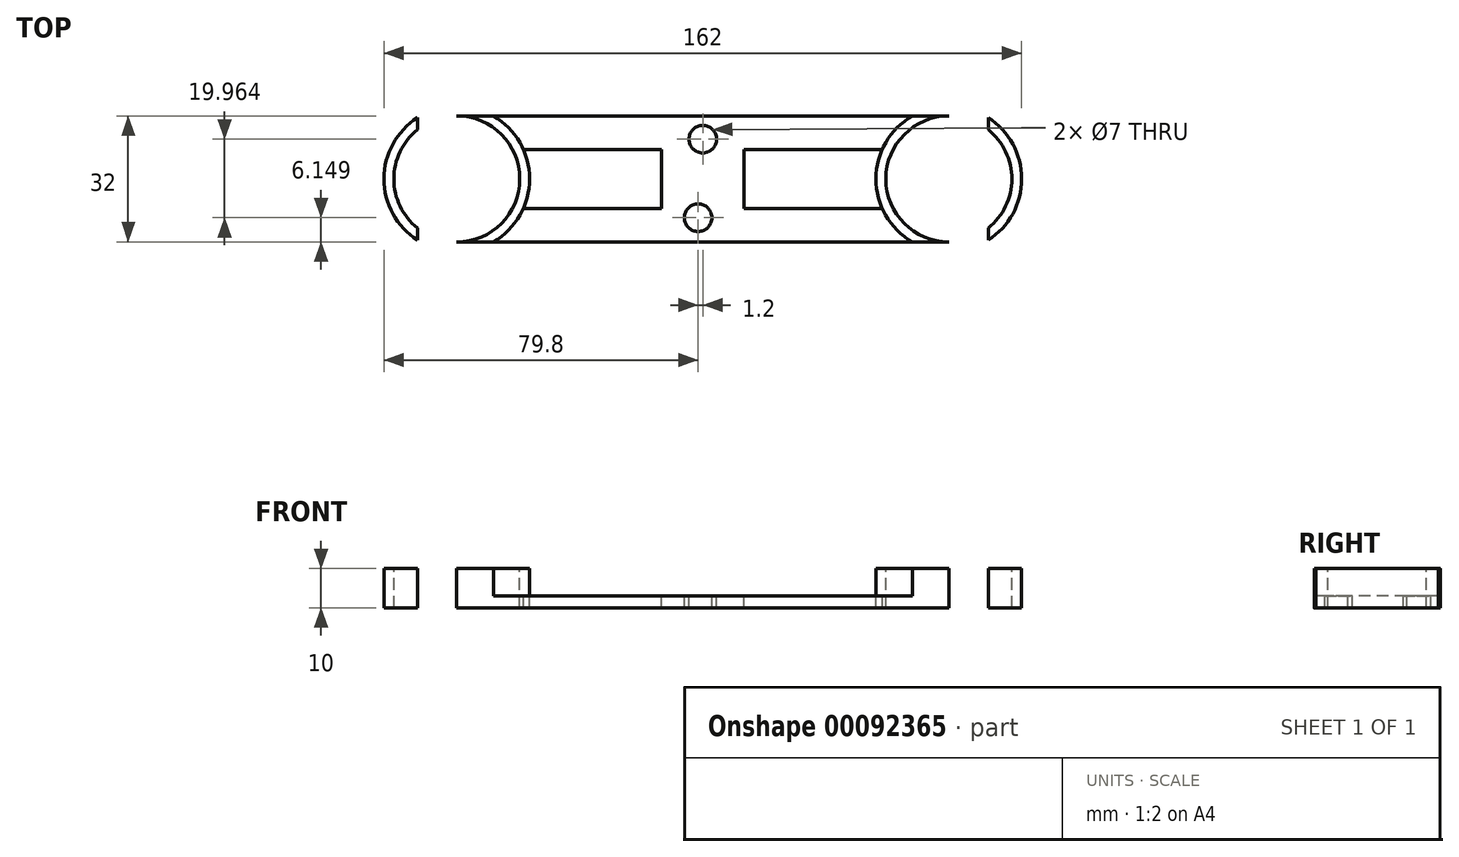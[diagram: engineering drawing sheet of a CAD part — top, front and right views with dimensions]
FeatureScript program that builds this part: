
annotation { "Feature Type Name" : "Feature", "Feature Type Description" : "" }
export const myFeature = defineFeature(function(context is Context, id is Id, definition is map)
    precondition{}
    {
        {
            var Q0;
            Q0=qCreatedBy(makeId("Top.planeOp"),FACE);
            var sketch = newSketch(context, id + "F0", { "sketchPlane" : qUnion([Q0])});
            skLineSegment(sketch, "E0.bottom", {"start": v(-62.5, 7.5) * mm, "end": v(62.5, 7.5) * mm});
            skLineSegment(sketch, "E0.top", {"start": v(-62.5, -7.5) * mm, "end": v(62.5, -7.5) * mm});
            skLineSegment(sketch, "E0.left", {"start": v(-62.5, 7.5) * mm, "end": v(-62.5, -7.5) * mm});
            skLineSegment(sketch, "E0.right", {"start": v(62.5, 7.5) * mm, "end": v(62.5, -7.5) * mm});
            skLineSegment(sketch, "E1", {"start": v(0, 7.5) * mm, "end": v(0, -7.5) * mm, "construction": true});
            skLineSegment(sketch, "E2", {"start": v(62.5, 0) * mm, "end": v(0, 0) * mm, "construction": true});
            skLineSegment(sketch, "E3", {"start": v(0, 0) * mm, "end": v(-62.5, 0) * mm, "construction": true});
            skLineSegment(sketch, "E4.bottom", {"start": v(-46.5, 7.5) * mm, "end": v(46.5, 7.5) * mm, "construction": true});
            skLineSegment(sketch, "E4.top", {"start": v(-46.5, -7.5) * mm, "end": v(46.5, -7.5) * mm, "construction": true});
            skLineSegment(sketch, "E4.left", {"start": v(-46.5, 7.5) * mm, "end": v(-46.5, -7.5) * mm, "construction": true});
            skLineSegment(sketch, "E4.right", {"start": v(46.5, 7.5) * mm, "end": v(46.5, -7.5) * mm, "construction": true});
            skLineSegment(sketch, "E5", {"start": v(-46.5, 18.61) * mm, "end": v(-62.5, 18.61) * mm, "construction": true});
            skLineSegment(sketch, "E6", {"start": v(46.5, 10.29) * mm, "end": v(62.5, 10.29) * mm, "construction": true});
            skCircle(sketch, "E7", {"center": v(62.5, 0) * mm, "radius": 16 * mm});
            skCircle(sketch, "E8", {"center": v(-62.5, 0) * mm, "radius": 16 * mm});
            skCircle(sketch, "E9", {"center": v(-62.5, 0) * mm, "radius": 18.5 * mm});
            skCircle(sketch, "E10", {"center": v(62.5, 0) * mm, "radius": 18.5 * mm});
            skLineSegment(sketch, "E11", {"start": v(-72.5, 15.56) * mm, "end": v(-72.5, -15.56) * mm});
            skLineSegment(sketch, "E12", {"start": v(-62.5, 0) * mm, "end": v(-72.5, 0) * mm, "construction": true});
            skLineSegment(sketch, "E13", {"start": v(72.5, 15.56) * mm, "end": v(72.5, -15.56) * mm});
            skLineSegment(sketch, "E14", {"start": v(62.5, 0) * mm, "end": v(72.5, 0) * mm, "construction": true});
            skLineSegment(sketch, "E15.top", {"start": v(-62.5, 16) * mm, "end": v(62.5, 16) * mm});
            skLineSegment(sketch, "E15.left", {"start": v(-62.5, 7.5) * mm, "end": v(-62.5, 16) * mm});
            skLineSegment(sketch, "E15.right", {"start": v(62.5, 7.5) * mm, "end": v(62.5, 16) * mm});
            skLineSegment(sketch, "E16.bottom", {"start": v(62.5, -7.5) * mm, "end": v(-62.5, -7.5) * mm});
            skLineSegment(sketch, "E16.top", {"start": v(62.5, -16) * mm, "end": v(-62.5, -16) * mm});
            skLineSegment(sketch, "E16.left", {"start": v(62.5, -7.5) * mm, "end": v(62.5, -16) * mm});
            skLineSegment(sketch, "E16.right", {"start": v(-62.5, -7.5) * mm, "end": v(-62.5, -16) * mm});
            skLineSegment(sketch, "E17", {"start": v(-10.45, 7.5) * mm, "end": v(-10.45, -7.5) * mm});
            skLineSegment(sketch, "E18", {"start": v(10.45, 7.5) * mm, "end": v(10.45, -7.5) * mm});
            skLineSegment(sketch, "E19", {"start": v(-10.45, 3.44) * mm, "end": v(0, 3.44) * mm, "construction": true});
            skLineSegment(sketch, "E20", {"start": v(0, 3.44) * mm, "end": v(10.45, 3.44) * mm, "construction": true});
            skSolve(sketch);
        }
        {
            var Q0;
            {var subQ3=sQuery(id+"F0.wireOp",EDGE,"E11");var subQ5=sQuery(id+"F0.wireOp",EDGE,"E9");var subQ6=makeQuery(id+"F0.imprint","INTERSECT",VERTEX,{"disambiguationData":[OD(0.0)],"derivedFrom":[subQ5,subQ3]});Q0=makeQuery(id+"F0.imprint","IMPRINT",FACE,{"disambiguationData":[TD([[makeQuery(id+"F0.imprint","IMPRINT",EDGE,{"disambiguationData":[TD([[subQ6,1.0]])],"derivedFrom":subQ5}),1.0]])]});}
            var Q1;
            {var subQ3=sQuery(id+"F0.wireOp",EDGE,"E11");var subQ5=sQuery(id+"F0.wireOp",EDGE,"E9");var subQ6=makeQuery(id+"F0.imprint","INTERSECT",VERTEX,{"disambiguationData":[OD(1.0)],"derivedFrom":[subQ5,subQ3]});Q1=makeQuery(id+"F0.imprint","IMPRINT",FACE,{"disambiguationData":[TD([[makeQuery(id+"F0.imprint","IMPRINT",EDGE,{"disambiguationData":[TD([[subQ6,-1.0]])],"derivedFrom":subQ5}),1.0]])]});}
            var Q2;
            {var subQ0=sQuery(id+"F0.wireOp",EDGE,"E15.top");var subQ5=sQuery(id+"F0.wireOp",EDGE,"E9");var subQ6=makeQuery(id+"F0.imprint","INTERSECT",VERTEX,{"derivedFrom":[subQ5,subQ0]});Q2=makeQuery(id+"F0.imprint","IMPRINT",FACE,{"disambiguationData":[TD([[makeQuery(id+"F0.imprint","IMPRINT",EDGE,{"disambiguationData":[TD([[subQ6,1.0]])],"derivedFrom":subQ5}),1.0]])]});}
            var Q3;
            {var subQ0=sQuery(id+"F0.wireOp",EDGE,"E16.top");var subQ5=sQuery(id+"F0.wireOp",EDGE,"E9");var subQ7=makeQuery(id+"F0.imprint","INTERSECT",VERTEX,{"derivedFrom":[subQ5,subQ0]});Q3=makeQuery(id+"F0.imprint","IMPRINT",FACE,{"disambiguationData":[TD([[makeQuery(id+"F0.imprint","IMPRINT",EDGE,{"disambiguationData":[TD([[subQ7,-1.0]])],"derivedFrom":subQ5}),1.0]])]});}
            var Q4;
            {var subQ0=sQuery(id+"F0.wireOp",EDGE,"E0.bottom");var subQ1=sQuery(id+"F0.wireOp",EDGE,"E8");var subQ2=makeQuery(id+"F0.imprint","INTERSECT",VERTEX,{"derivedFrom":[subQ1,subQ0]});Q4=makeQuery(id+"F0.imprint","IMPRINT",FACE,{"disambiguationData":[TD([[makeQuery(id+"F0.imprint","IMPRINT",EDGE,{"disambiguationData":[TD([[subQ2,1.0]])],"derivedFrom":subQ1}),-1.0]])]});}
            var Q5;
            {var subQ3=sQuery(id+"F0.wireOp",EDGE,"E11");var subQ5=sQuery(id+"F0.wireOp",EDGE,"E9");var subQ6=makeQuery(id+"F0.imprint","INTERSECT",VERTEX,{"disambiguationData":[OD(1.0)],"derivedFrom":[subQ5,subQ3]});Q5=makeQuery(id+"F0.imprint","IMPRINT",FACE,{"disambiguationData":[TD([[makeQuery(id+"F0.imprint","IMPRINT",EDGE,{"disambiguationData":[TD([[subQ6,-1.0]])],"derivedFrom":subQ5}),1.0]])]});}
            var Q6;
            {var subQ3=sQuery(id+"F0.wireOp",EDGE,"E11");var subQ5=sQuery(id+"F0.wireOp",EDGE,"E9");var subQ6=makeQuery(id+"F0.imprint","INTERSECT",VERTEX,{"disambiguationData":[OD(0.0)],"derivedFrom":[subQ5,subQ3]});Q6=makeQuery(id+"F0.imprint","IMPRINT",FACE,{"disambiguationData":[TD([[makeQuery(id+"F0.imprint","IMPRINT",EDGE,{"disambiguationData":[TD([[subQ6,1.0]])],"derivedFrom":subQ5}),1.0]])]});}
            var Q7;
            {var subQ3=sQuery(id+"F0.wireOp",EDGE,"E13");var subQ5=sQuery(id+"F0.wireOp",EDGE,"E10");var subQ7=makeQuery(id+"F0.imprint","INTERSECT",VERTEX,{"disambiguationData":[OD(0.0)],"derivedFrom":[subQ5,subQ3]});Q7=makeQuery(id+"F0.imprint","IMPRINT",FACE,{"disambiguationData":[TD([[makeQuery(id+"F0.imprint","IMPRINT",EDGE,{"disambiguationData":[TD([[subQ7,-1.0]])],"derivedFrom":subQ5}),1.0]])]});}
            var Q8;
            {var subQ3=sQuery(id+"F0.wireOp",EDGE,"E13");var subQ5=sQuery(id+"F0.wireOp",EDGE,"E10");var subQ7=makeQuery(id+"F0.imprint","INTERSECT",VERTEX,{"disambiguationData":[OD(0.0)],"derivedFrom":[subQ5,subQ3]});Q8=makeQuery(id+"F0.imprint","IMPRINT",FACE,{"disambiguationData":[TD([[makeQuery(id+"F0.imprint","IMPRINT",EDGE,{"disambiguationData":[TD([[subQ7,-1.0]])],"derivedFrom":subQ5}),1.0]])]});}
            var Q9;
            {var subQ3=sQuery(id+"F0.wireOp",EDGE,"E13");var subQ5=sQuery(id+"F0.wireOp",EDGE,"E10");var subQ6=makeQuery(id+"F0.imprint","INTERSECT",VERTEX,{"disambiguationData":[OD(1.0)],"derivedFrom":[subQ5,subQ3]});Q9=makeQuery(id+"F0.imprint","IMPRINT",FACE,{"disambiguationData":[TD([[makeQuery(id+"F0.imprint","IMPRINT",EDGE,{"disambiguationData":[TD([[subQ6,1.0]])],"derivedFrom":subQ5}),1.0]])]});}
            var Q10;
            {var subQ0=sQuery(id+"F0.wireOp",EDGE,"E15.top");var subQ5=sQuery(id+"F0.wireOp",EDGE,"E10");var subQ6=makeQuery(id+"F0.imprint","INTERSECT",VERTEX,{"derivedFrom":[subQ5,subQ0]});Q10=makeQuery(id+"F0.imprint","IMPRINT",FACE,{"disambiguationData":[TD([[makeQuery(id+"F0.imprint","IMPRINT",EDGE,{"disambiguationData":[TD([[subQ6,-1.0]])],"derivedFrom":subQ5}),1.0]])]});}
            var Q11;
            {var subQ0=sQuery(id+"F0.wireOp",EDGE,"E0.bottom");var subQ1=sQuery(id+"F0.wireOp",EDGE,"E7");var subQ2=makeQuery(id+"F0.imprint","INTERSECT",VERTEX,{"derivedFrom":[subQ1,subQ0]});Q11=makeQuery(id+"F0.imprint","IMPRINT",FACE,{"disambiguationData":[TD([[makeQuery(id+"F0.imprint","IMPRINT",EDGE,{"disambiguationData":[TD([[subQ2,-1.0]])],"derivedFrom":subQ1}),-1.0]])]});}
            var Q12;
            {var subQ0=sQuery(id+"F0.wireOp",EDGE,"E16.top");var subQ5=sQuery(id+"F0.wireOp",EDGE,"E10");var subQ6=makeQuery(id+"F0.imprint","INTERSECT",VERTEX,{"derivedFrom":[subQ5,subQ0]});Q12=makeQuery(id+"F0.imprint","IMPRINT",FACE,{"disambiguationData":[TD([[makeQuery(id+"F0.imprint","IMPRINT",EDGE,{"disambiguationData":[TD([[subQ6,1.0]])],"derivedFrom":subQ5}),1.0]])]});}
            var Q13;
            {var subQ3=sQuery(id+"F0.wireOp",EDGE,"E13");var subQ5=sQuery(id+"F0.wireOp",EDGE,"E10");var subQ6=makeQuery(id+"F0.imprint","INTERSECT",VERTEX,{"disambiguationData":[OD(1.0)],"derivedFrom":[subQ5,subQ3]});Q13=makeQuery(id+"F0.imprint","IMPRINT",FACE,{"disambiguationData":[TD([[makeQuery(id+"F0.imprint","IMPRINT",EDGE,{"disambiguationData":[TD([[subQ6,1.0]])],"derivedFrom":subQ5}),1.0]])]});}
            var Q14;
            {var subQ0=sQuery(id+"F0.wireOp",EDGE,"E16.top");var subQ1=sQuery(id+"F0.wireOp",EDGE,"E9");var subQ2=makeQuery(id+"F0.imprint","INTERSECT",VERTEX,{"derivedFrom":[subQ1,subQ0]});Q14=makeQuery(id+"F0.imprint","IMPRINT",FACE,{"disambiguationData":[TD([[makeQuery(id+"F0.imprint","IMPRINT",EDGE,{"disambiguationData":[TD([[subQ2,-1.0]])],"derivedFrom":subQ1}),-1.0]])]});}
            var Q15;
            {var subQ0=sQuery(id+"F0.wireOp",EDGE,"E15.top");var subQ1=sQuery(id+"F0.wireOp",EDGE,"E9");var subQ2=makeQuery(id+"F0.imprint","INTERSECT",VERTEX,{"derivedFrom":[subQ1,subQ0]});Q15=makeQuery(id+"F0.imprint","IMPRINT",FACE,{"disambiguationData":[TD([[makeQuery(id+"F0.imprint","IMPRINT",EDGE,{"disambiguationData":[TD([[subQ2,1.0]])],"derivedFrom":subQ1}),-1.0]])]});}
            var Q16;
            {var subQ0=sQuery(id+"F0.wireOp",EDGE,"E17");Q16=makeQuery(id+"F0.imprint","IMPRINT",FACE,{"disambiguationData":[TD([[makeQuery(id+"F0.imprint","IMPRINT",EDGE,{"derivedFrom":subQ0}),1.0]])]});}
            extrude(context, id + "F1", {"entities" : qUnion([Q0, Q1, Q2, Q3, Q4, Q5, Q6, Q7, Q8, Q9, Q10, Q11, Q12, Q13, Q14, Q15, Q16]), "oppositeDirection" : true, "depth" : 5 * mm});
        }
        {
            var Q0;
            {var subQ3=sQuery(id+"F0.wireOp",EDGE,"E11");var subQ5=sQuery(id+"F0.wireOp",EDGE,"E9");var subQ6=makeQuery(id+"F0.imprint","INTERSECT",VERTEX,{"disambiguationData":[OD(0.0)],"derivedFrom":[subQ5,subQ3]});Q0=makeQuery(id+"F0.imprint","IMPRINT",FACE,{"disambiguationData":[TD([[makeQuery(id+"F0.imprint","IMPRINT",EDGE,{"disambiguationData":[TD([[subQ6,1.0]])],"derivedFrom":subQ5}),1.0]])]});}
            var Q1;
            {var subQ3=sQuery(id+"F0.wireOp",EDGE,"E11");var subQ5=sQuery(id+"F0.wireOp",EDGE,"E9");var subQ6=makeQuery(id+"F0.imprint","INTERSECT",VERTEX,{"disambiguationData":[OD(1.0)],"derivedFrom":[subQ5,subQ3]});Q1=makeQuery(id+"F0.imprint","IMPRINT",FACE,{"disambiguationData":[TD([[makeQuery(id+"F0.imprint","IMPRINT",EDGE,{"disambiguationData":[TD([[subQ6,-1.0]])],"derivedFrom":subQ5}),1.0]])]});}
            var Q2;
            {var subQ0=sQuery(id+"F0.wireOp",EDGE,"E15.top");var subQ5=sQuery(id+"F0.wireOp",EDGE,"E9");var subQ6=makeQuery(id+"F0.imprint","INTERSECT",VERTEX,{"derivedFrom":[subQ5,subQ0]});Q2=makeQuery(id+"F0.imprint","IMPRINT",FACE,{"disambiguationData":[TD([[makeQuery(id+"F0.imprint","IMPRINT",EDGE,{"disambiguationData":[TD([[subQ6,1.0]])],"derivedFrom":subQ5}),1.0]])]});}
            var Q3;
            {var subQ0=sQuery(id+"F0.wireOp",EDGE,"E16.top");var subQ5=sQuery(id+"F0.wireOp",EDGE,"E9");var subQ7=makeQuery(id+"F0.imprint","INTERSECT",VERTEX,{"derivedFrom":[subQ5,subQ0]});Q3=makeQuery(id+"F0.imprint","IMPRINT",FACE,{"disambiguationData":[TD([[makeQuery(id+"F0.imprint","IMPRINT",EDGE,{"disambiguationData":[TD([[subQ7,-1.0]])],"derivedFrom":subQ5}),1.0]])]});}
            var Q4;
            {var subQ0=sQuery(id+"F0.wireOp",EDGE,"E0.bottom");var subQ1=sQuery(id+"F0.wireOp",EDGE,"E8");var subQ2=makeQuery(id+"F0.imprint","INTERSECT",VERTEX,{"derivedFrom":[subQ1,subQ0]});Q4=makeQuery(id+"F0.imprint","IMPRINT",FACE,{"disambiguationData":[TD([[makeQuery(id+"F0.imprint","IMPRINT",EDGE,{"disambiguationData":[TD([[subQ2,1.0]])],"derivedFrom":subQ1}),-1.0]])]});}
            var Q5;
            {var subQ3=sQuery(id+"F0.wireOp",EDGE,"E11");var subQ5=sQuery(id+"F0.wireOp",EDGE,"E9");var subQ6=makeQuery(id+"F0.imprint","INTERSECT",VERTEX,{"disambiguationData":[OD(0.0)],"derivedFrom":[subQ5,subQ3]});Q5=makeQuery(id+"F0.imprint","IMPRINT",FACE,{"disambiguationData":[TD([[makeQuery(id+"F0.imprint","IMPRINT",EDGE,{"disambiguationData":[TD([[subQ6,1.0]])],"derivedFrom":subQ5}),1.0]])]});}
            var Q6;
            {var subQ3=sQuery(id+"F0.wireOp",EDGE,"E11");var subQ5=sQuery(id+"F0.wireOp",EDGE,"E9");var subQ6=makeQuery(id+"F0.imprint","INTERSECT",VERTEX,{"disambiguationData":[OD(1.0)],"derivedFrom":[subQ5,subQ3]});Q6=makeQuery(id+"F0.imprint","IMPRINT",FACE,{"disambiguationData":[TD([[makeQuery(id+"F0.imprint","IMPRINT",EDGE,{"disambiguationData":[TD([[subQ6,-1.0]])],"derivedFrom":subQ5}),1.0]])]});}
            var Q7;
            {var subQ3=sQuery(id+"F0.wireOp",EDGE,"E13");var subQ5=sQuery(id+"F0.wireOp",EDGE,"E10");var subQ6=makeQuery(id+"F0.imprint","INTERSECT",VERTEX,{"disambiguationData":[OD(1.0)],"derivedFrom":[subQ5,subQ3]});Q7=makeQuery(id+"F0.imprint","IMPRINT",FACE,{"disambiguationData":[TD([[makeQuery(id+"F0.imprint","IMPRINT",EDGE,{"disambiguationData":[TD([[subQ6,1.0]])],"derivedFrom":subQ5}),1.0]])]});}
            var Q8;
            {var subQ3=sQuery(id+"F0.wireOp",EDGE,"E13");var subQ5=sQuery(id+"F0.wireOp",EDGE,"E10");var subQ7=makeQuery(id+"F0.imprint","INTERSECT",VERTEX,{"disambiguationData":[OD(0.0)],"derivedFrom":[subQ5,subQ3]});Q8=makeQuery(id+"F0.imprint","IMPRINT",FACE,{"disambiguationData":[TD([[makeQuery(id+"F0.imprint","IMPRINT",EDGE,{"disambiguationData":[TD([[subQ7,-1.0]])],"derivedFrom":subQ5}),1.0]])]});}
            var Q9;
            {var subQ3=sQuery(id+"F0.wireOp",EDGE,"E13");var subQ5=sQuery(id+"F0.wireOp",EDGE,"E10");var subQ6=makeQuery(id+"F0.imprint","INTERSECT",VERTEX,{"disambiguationData":[OD(1.0)],"derivedFrom":[subQ5,subQ3]});Q9=makeQuery(id+"F0.imprint","IMPRINT",FACE,{"disambiguationData":[TD([[makeQuery(id+"F0.imprint","IMPRINT",EDGE,{"disambiguationData":[TD([[subQ6,1.0]])],"derivedFrom":subQ5}),1.0]])]});}
            var Q10;
            {var subQ0=sQuery(id+"F0.wireOp",EDGE,"E15.top");var subQ5=sQuery(id+"F0.wireOp",EDGE,"E10");var subQ6=makeQuery(id+"F0.imprint","INTERSECT",VERTEX,{"derivedFrom":[subQ5,subQ0]});Q10=makeQuery(id+"F0.imprint","IMPRINT",FACE,{"disambiguationData":[TD([[makeQuery(id+"F0.imprint","IMPRINT",EDGE,{"disambiguationData":[TD([[subQ6,-1.0]])],"derivedFrom":subQ5}),1.0]])]});}
            var Q11;
            {var subQ0=sQuery(id+"F0.wireOp",EDGE,"E0.bottom");var subQ1=sQuery(id+"F0.wireOp",EDGE,"E7");var subQ2=makeQuery(id+"F0.imprint","INTERSECT",VERTEX,{"derivedFrom":[subQ1,subQ0]});Q11=makeQuery(id+"F0.imprint","IMPRINT",FACE,{"disambiguationData":[TD([[makeQuery(id+"F0.imprint","IMPRINT",EDGE,{"disambiguationData":[TD([[subQ2,-1.0]])],"derivedFrom":subQ1}),-1.0]])]});}
            var Q12;
            {var subQ0=sQuery(id+"F0.wireOp",EDGE,"E16.top");var subQ5=sQuery(id+"F0.wireOp",EDGE,"E10");var subQ6=makeQuery(id+"F0.imprint","INTERSECT",VERTEX,{"derivedFrom":[subQ5,subQ0]});Q12=makeQuery(id+"F0.imprint","IMPRINT",FACE,{"disambiguationData":[TD([[makeQuery(id+"F0.imprint","IMPRINT",EDGE,{"disambiguationData":[TD([[subQ6,1.0]])],"derivedFrom":subQ5}),1.0]])]});}
            var Q13;
            {var subQ3=sQuery(id+"F0.wireOp",EDGE,"E13");var subQ5=sQuery(id+"F0.wireOp",EDGE,"E10");var subQ7=makeQuery(id+"F0.imprint","INTERSECT",VERTEX,{"disambiguationData":[OD(0.0)],"derivedFrom":[subQ5,subQ3]});Q13=makeQuery(id+"F0.imprint","IMPRINT",FACE,{"disambiguationData":[TD([[makeQuery(id+"F0.imprint","IMPRINT",EDGE,{"disambiguationData":[TD([[subQ7,-1.0]])],"derivedFrom":subQ5}),1.0]])]});}
            extrude(context, id + "F2", {"entities" : qUnion([Q0, Q1, Q2, Q3, Q4, Q5, Q6, Q7, Q8, Q9, Q10, Q11, Q12, Q13]), "operationType" : NewBodyOperationType.ADD, "depth" : 5 * mm});
        }
        {
            var Q0;
            Q0=makeQuery(id+"F1.opExtrude","CAP_FACE",FACE,{"disambiguationData":[OSD([sQuery(id+"F0.wireOp",EDGE,"E7"),sQuery(id+"F0.wireOp",EDGE,"E8"),sQuery(id+"F0.wireOp",EDGE,"E9"),sQuery(id+"F0.wireOp",EDGE,"E10"),sQuery(id+"F0.wireOp",EDGE,"E11"),sQuery(id+"F0.wireOp",EDGE,"E13"),sQuery(id+"F0.wireOp",EDGE,"E0.bottom"),sQuery(id+"F0.wireOp",EDGE,"E15.top"),sQuery(id+"F0.wireOp",EDGE,"E16.bottom"),sQuery(id+"F0.wireOp",EDGE,"E16.top"),sQuery(id+"F0.wireOp",EDGE,"E17"),sQuery(id+"F0.wireOp",EDGE,"E18")])],"isStart":true});
            var sketch = newSketch(context, id + "F3", { "sketchPlane" : qUnion([Q0])});
            skCircle(sketch, "E21", {"center": v(0, 10.11) * mm, "radius": 3.5 * mm});
            skCircle(sketch, "E22", {"center": v(-1.2, -9.85) * mm, "radius": 3.5 * mm});
            skLineSegment(sketch, "E23", {"start": v(0, 10.11) * mm, "end": v(-1.2, -9.85) * mm, "construction": true});
            skSolve(sketch);
        }
        {
            var Q0;
            Q0=makeQuery(id+"F3.imprint","IMPRINT",FACE,{"disambiguationData":[TD([[makeQuery(id+"F3.imprint","IMPRINT",EDGE,{"derivedFrom":sQuery(id+"F3.wireOp",EDGE,"E21")}),-1.0]])]});
            var Q1;
            Q1=makeQuery(id+"F3.imprint","IMPRINT",FACE,{"disambiguationData":[TD([[makeQuery(id+"F3.imprint","IMPRINT",EDGE,{"derivedFrom":sQuery(id+"F3.wireOp",EDGE,"E22")}),-1.0]])]});
            extrude(context, id + "F4", {"entities" : qUnion([Q0, Q1]), "operationType" : NewBodyOperationType.REMOVE, "oppositeDirection" : true, "depth" : 2 * mm});
        }
        {
            var Q0;
            Q0=makeQuery(id+"F4.boolean.opBoolean","SPLIT",FACE,{"disambiguationData":[TD([makeQuery(id+"F4.opExtrude","SWEPT_FACE",FACE,{"disambiguationData":[OSD([sQuery(id+"F3.wireOp",EDGE,"E21")])]})])],"derivedFrom":makeQuery(id+"F1.opExtrude","CAP_FACE",FACE,{"disambiguationData":[OSD([sQuery(id+"F0.wireOp",EDGE,"E7"),sQuery(id+"F0.wireOp",EDGE,"E8"),sQuery(id+"F0.wireOp",EDGE,"E9"),sQuery(id+"F0.wireOp",EDGE,"E10"),sQuery(id+"F0.wireOp",EDGE,"E11"),sQuery(id+"F0.wireOp",EDGE,"E13"),sQuery(id+"F0.wireOp",EDGE,"E0.bottom"),sQuery(id+"F0.wireOp",EDGE,"E15.top"),sQuery(id+"F0.wireOp",EDGE,"E16.bottom"),sQuery(id+"F0.wireOp",EDGE,"E16.top"),sQuery(id+"F0.wireOp",EDGE,"E17"),sQuery(id+"F0.wireOp",EDGE,"E18")])],"isStart":true})});
            var Q1;
            Q1=makeQuery(id+"F4.boolean.opBoolean","SPLIT",FACE,{"disambiguationData":[TD([makeQuery(id+"F4.opExtrude","SWEPT_FACE",FACE,{"disambiguationData":[OSD([sQuery(id+"F3.wireOp",EDGE,"E22")])]})])],"derivedFrom":makeQuery(id+"F1.opExtrude","CAP_FACE",FACE,{"disambiguationData":[OSD([sQuery(id+"F0.wireOp",EDGE,"E7"),sQuery(id+"F0.wireOp",EDGE,"E8"),sQuery(id+"F0.wireOp",EDGE,"E9"),sQuery(id+"F0.wireOp",EDGE,"E10"),sQuery(id+"F0.wireOp",EDGE,"E11"),sQuery(id+"F0.wireOp",EDGE,"E13"),sQuery(id+"F0.wireOp",EDGE,"E0.bottom"),sQuery(id+"F0.wireOp",EDGE,"E15.top"),sQuery(id+"F0.wireOp",EDGE,"E16.bottom"),sQuery(id+"F0.wireOp",EDGE,"E16.top"),sQuery(id+"F0.wireOp",EDGE,"E17"),sQuery(id+"F0.wireOp",EDGE,"E18")])],"isStart":true})});
            extrude(context, id + "F5", {"entities" : qUnion([Q0, Q1]), "operationType" : NewBodyOperationType.REMOVE, "endBound" : BoundingType.UP_TO_NEXT, "oppositeDirection" : true, "depth" : 25 * mm});
        }
    });
